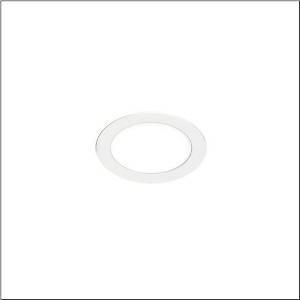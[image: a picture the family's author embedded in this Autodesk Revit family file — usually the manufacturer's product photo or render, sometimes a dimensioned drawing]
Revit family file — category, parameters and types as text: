
# Revit family: lunis_41_flat_51dr10mdhbb
name_source: partatom
category: Lighting Fixtures
units: mm (PartAtom-declared; Revit-internal decimal feet)

## family parameters
Cut with Voids When Loaded = No
Host = Face
Light Source = No
Part Type = Normal
Room Calculation Point = No
Round Connector Dimension = Use Diameter
Shared = No

## types (1)
- --- (1 x LED, 1600 lm, 12.5 W, 6500K)
    Apparent Load = 13 VA
    CIE Flux Codes = 49 80 96 100 100
    Color Rendering = 80
    Color Temperature = 6500K
    Default Elevation = 1800 mm
    Description = Lunis 41,  Flat, downlight, light emission: direct distribution, LED rated luminous flux: 1.580lm, light colour: 840/865, mains connection: 230V, AC, 50/60Hz, housing, round, of aluminium, coated, traffic white (RAL 9016), diameter: 170mm, protection rating (complete): IP20, protection rating (on room side): IP44, insulation class (complete): insulation class II (safety insulation), certification: CE, permissible ambient temperature for indoor applications: -20..+40°C, packaging unit: 1 piece
    Height = 0 mm  [stored 0 ft]
    Lamp = 1 x LED
    Lamp Light Flux = 1600 lm
    Lamp Power = 12.5 W
    Lamp count = 1
    Length = 170 mm  [stored 0.557743 ft]
    Luminous efficacy = 128 lm/W
    Manufacturer = Siteco
    ModVariant = No
    Model = 51DR10MDHBB
    Mounting Place = Ceiling
    Mounting Type = Recessed
    Number of Poles = 1
    OnlyDefault = Yes
    Power Factor = 1
    Product Name = Lunis 41 Flat
    Product group = downlight
    ProductGroupID = 400
    Protection Class = Protection class II
    Protection Degree = IP 20
    RLX_Detail_Level = 1
    RLX_Emergency_Light_Flux = 0 lm
    RLX_Emergency_Type = 0
    RLX_Emergency_Type_DB = No
    RlxData = <blob elided: 9777 chars, md5=d6529b84>
    Socket = socket
    Standby Power = 0 W
    System Light Flux = 1600 lm
    System Power = 13 W
    Type Comments = individual setting: colour temperature 6500K
    Type Image = l_1340921.jpg
    URL = http://relux.com
    VarID = @adj_001623
    Voltage = 0 V
    Weight = 0.00 kg
    Width = 0 mm  [stored 0 ft]

note: [stored X ft] marks values corroborated as IEEE doubles in the binary element streams (Revit-internal decimal feet)

## geometry (parser evidence)
native form markers: Sweep x8
no freeform markers — native parametric forms only
